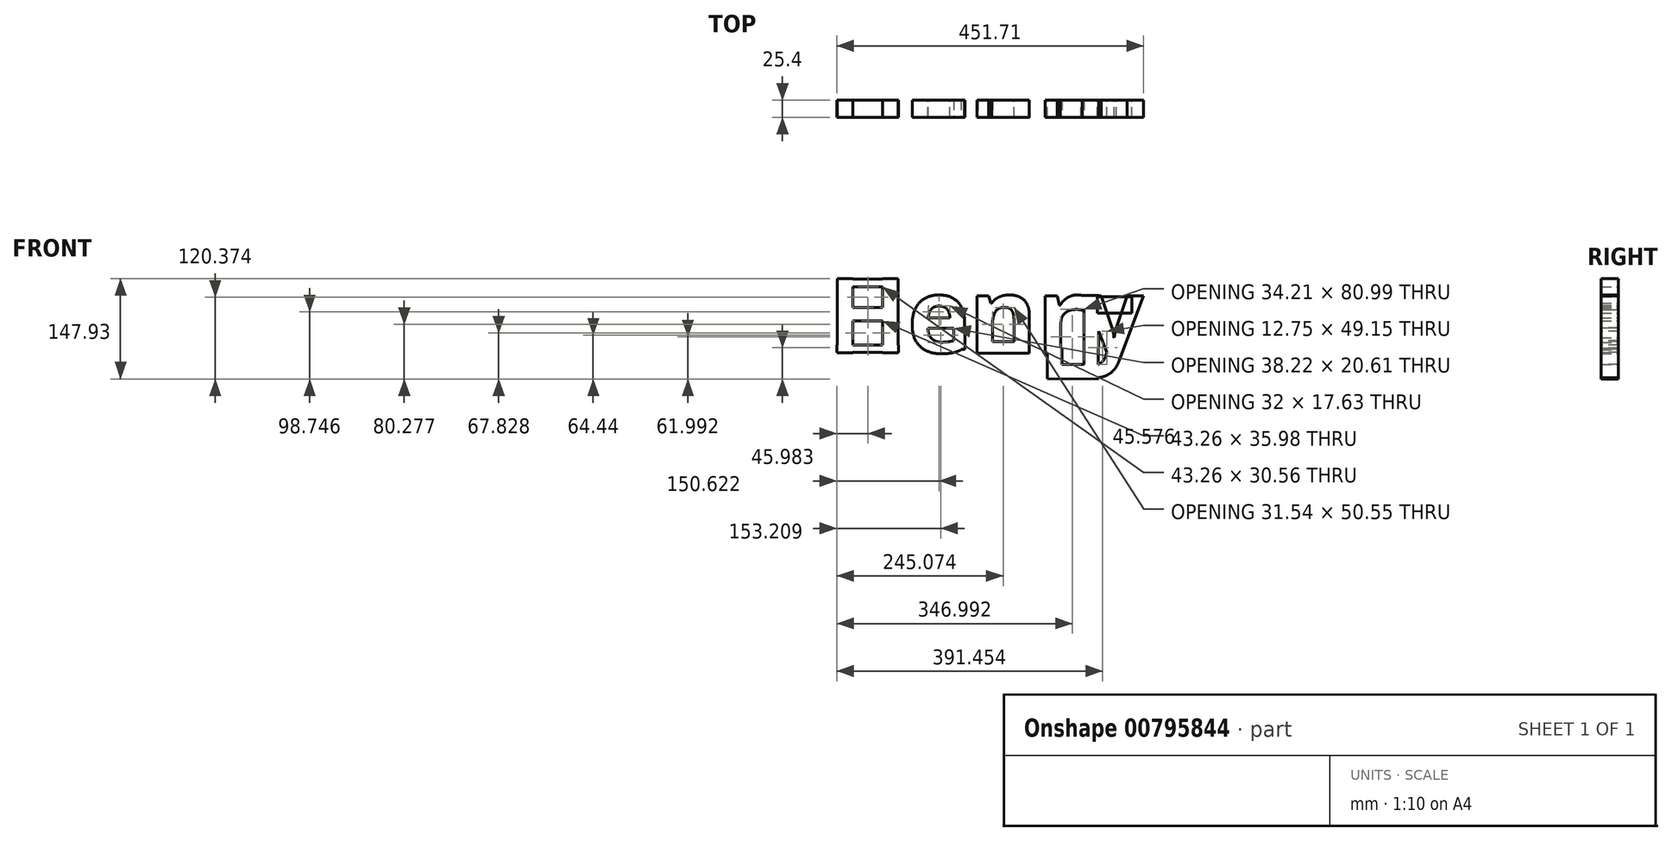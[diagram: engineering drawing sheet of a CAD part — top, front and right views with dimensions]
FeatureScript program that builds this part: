
annotation { "Feature Type Name" : "Feature", "Feature Type Description" : "" }
export const myFeature = defineFeature(function(context is Context, id is Id, definition is map)
    precondition{}
    {
        {
            var Q0;
            Q0=qCreatedBy(makeId("Front.planeOp"),FACE);
            var sketch = newSketch(context, id + "F0", { "sketchPlane" : qUnion([Q0])});
            skText(sketch, "E0", { "text": "Henry", "fontName": "OpenSans-Bold.ttf"});
            const initialGuessF0  = {"E0": [-0.05237, -0.07557, 1, 0, 0.1102]};
            skSetInitialGuess(sketch, initialGuessF0);
            skSolve(sketch);
        }
        {
            var Q0;
            Q0 = qSketchRegion(id + "F0", true);
            extrude(context, id + "F1", {"entities" : qUnion([Q0]), "depth" : 25.4 * mm, "offsetDistance" : 25.4 * mm});
        }
        {
            var Q0;
            Q0=qCreatedBy(makeId("Front.planeOp"),FACE);
            var sketch = newSketch(context, id + "F2", { "sketchPlane" : qUnion([Q0])});
            skLineSegment(sketch, "E1.bottom", {"start": v(-37.51, 33.02) * mm, "end": v(50.67, 33.02) * mm});
            skLineSegment(sketch, "E1.top", {"start": v(-37.51, 21.42) * mm, "end": v(50.67, 21.42) * mm});
            skLineSegment(sketch, "E1.left", {"start": v(-37.51, 33.02) * mm, "end": v(-37.51, 21.42) * mm});
            skLineSegment(sketch, "E1.right", {"start": v(50.67, 33.02) * mm, "end": v(50.67, 21.42) * mm});
            skLineSegment(sketch, "E2.bottom", {"start": v(-39.4, -64.4) * mm, "end": v(51.6, -64.4) * mm});
            skLineSegment(sketch, "E2.top", {"start": v(-39.4, -75.06) * mm, "end": v(51.6, -75.06) * mm});
            skLineSegment(sketch, "E2.left", {"start": v(-39.4, -64.4) * mm, "end": v(-39.4, -75.06) * mm});
            skLineSegment(sketch, "E2.right", {"start": v(51.6, -64.4) * mm, "end": v(51.6, -75.06) * mm});
            skSolve(sketch);
        }
        {
            var Q0;
            Q0 = qSketchRegion(id + "F2", true);
            extrude(context, id + "F3", {"entities" : qUnion([Q0]), "operationType" : NewBodyOperationType.ADD, "depth" : 25.4 * mm, "offsetDistance" : 25.4 * mm});
        }
        {
            var Q0;
            Q0=qCreatedBy(makeId("Front.planeOp"),FACE);
            var sketch = newSketch(context, id + "F4", { "sketchPlane" : qUnion([Q0])});
            skLineSegment(sketch, "E3.bottom", {"start": v(132.93, -38.6) * mm, "end": v(149.09, -38.6) * mm});
            skLineSegment(sketch, "E3.top", {"start": v(132.93, -70.6) * mm, "end": v(149.09, -70.6) * mm});
            skLineSegment(sketch, "E3.left", {"start": v(132.93, -38.6) * mm, "end": v(132.93, -70.6) * mm});
            skLineSegment(sketch, "E3.right", {"start": v(149.09, -38.6) * mm, "end": v(149.09, -70.6) * mm});
            skSolve(sketch);
        }
        {
            var Q0;
            Q0 = qSketchRegion(id + "F4", true);
            extrude(context, id + "F5", {"entities" : qUnion([Q0]), "operationType" : NewBodyOperationType.ADD, "depth" : 25.4 * mm, "offsetDistance" : 25.4 * mm});
        }
        {
            var Q0;
            Q0=qCreatedBy(makeId("Front.planeOp"),FACE);
            var sketch = newSketch(context, id + "F6", { "sketchPlane" : qUnion([Q0])});
            skLineSegment(sketch, "E4.bottom", {"start": v(168.5, -59.23) * mm, "end": v(244.18, -59.23) * mm});
            skLineSegment(sketch, "E4.top", {"start": v(168.5, -76.16) * mm, "end": v(244.18, -76.16) * mm});
            skLineSegment(sketch, "E4.left", {"start": v(168.5, -59.23) * mm, "end": v(168.5, -76.16) * mm});
            skLineSegment(sketch, "E4.right", {"start": v(244.18, -59.23) * mm, "end": v(244.18, -76.16) * mm});
            skSolve(sketch);
        }
        {
            var Q0;
            Q0 = qSketchRegion(id + "F6", true);
            extrude(context, id + "F7", {"entities" : qUnion([Q0]), "operationType" : NewBodyOperationType.ADD, "depth" : 25.4 * mm, "offsetDistance" : 25.4 * mm});
        }
        {
            var Q0;
            Q0=qCreatedBy(makeId("Front.planeOp"),FACE);
            var sketch = newSketch(context, id + "F8", { "sketchPlane" : qUnion([Q0])});
            skLineSegment(sketch, "E5", {"start": v(279.72, -67.46) * mm, "end": v(279.72, -104.92) * mm});
            skLineSegment(sketch, "E6", {"start": v(279.72, -104.92) * mm, "end": v(336.76, -105.3) * mm});
            skLineSegment(sketch, "E7", {"start": v(336.76, -105.3) * mm, "end": v(337.25, 0) * mm});
            skLineSegment(sketch, "E8", {"start": v(337.25, 0) * mm, "end": v(320.93, 0) * mm});
            skSolve(sketch);
        }
        {
            var Q0;
            Q0=makeQuery(id+"F1.opExtrude","SWEPT_FACE",FACE,{"disambiguationData":[OSD([sQuery(id+"F0.wireOp",EDGE,"E0.sketch_text.stroke-50")])]});
            var Q1;
            Q1=sQuery(id+"F8.wireOp",EDGE,"E8");
            var Q2;
            Q2=sQuery(id+"F8.wireOp",EDGE,"E7");
            var Q3;
            Q3=sQuery(id+"F8.wireOp",EDGE,"E6");
            var Q4;
            Q4=sQuery(id+"F8.wireOp",EDGE,"E5");
            sweep(context, id + "F9", {"operationType" : NewBodyOperationType.ADD, "profiles" : qUnion([Q0]), "path" : qUnion([Q1, Q2, Q3, Q4])});
        }
        {
            var Q0;
            Q0=qCreatedBy(makeId("Front.planeOp"),FACE);
            var sketch = newSketch(context, id + "F10", { "sketchPlane" : qUnion([Q0])});
            skLineSegment(sketch, "E9.bottom", {"start": v(344.38, 6.6) * mm, "end": v(394.92, 6.6) * mm});
            skLineSegment(sketch, "E9.top", {"start": v(344.38, -17.17) * mm, "end": v(394.92, -17.17) * mm});
            skLineSegment(sketch, "E9.left", {"start": v(344.38, 6.6) * mm, "end": v(344.38, -17.17) * mm});
            skLineSegment(sketch, "E9.right", {"start": v(394.92, 6.6) * mm, "end": v(394.92, -17.17) * mm});
            skSolve(sketch);
        }
        {
            var Q0;
            Q0 = qSketchRegion(id + "F10", true);
            extrude(context, id + "F11", {"entities" : qUnion([Q0]), "depth" : 25.4 * mm, "offsetDistance" : 25.4 * mm});
        }
    });
